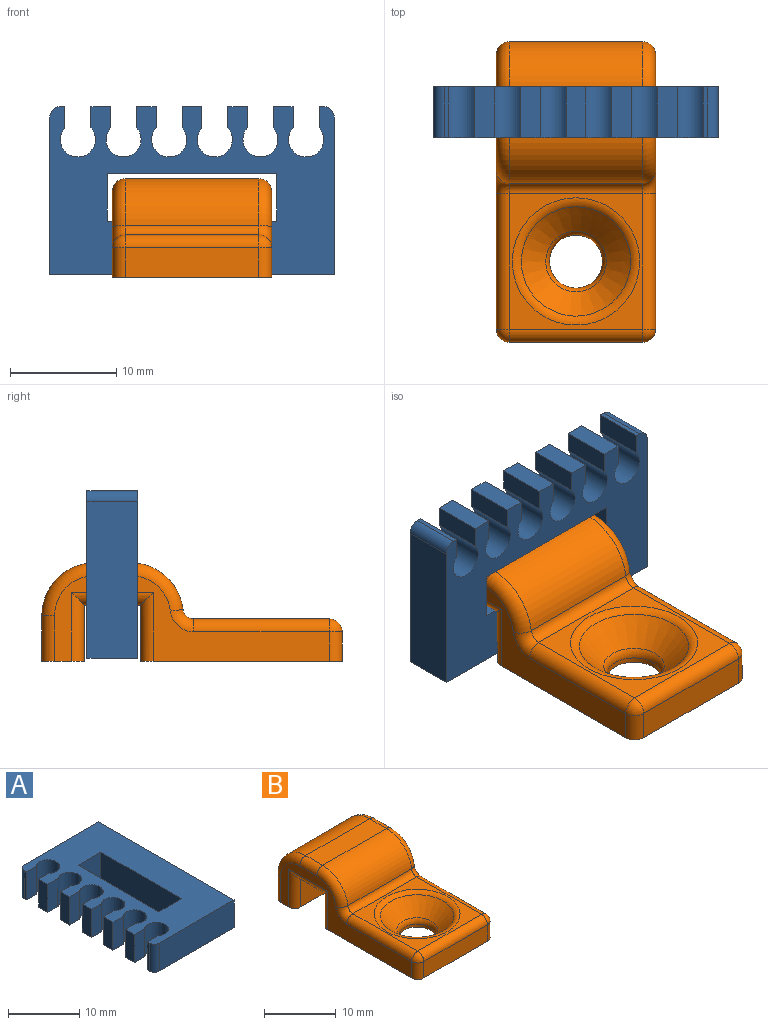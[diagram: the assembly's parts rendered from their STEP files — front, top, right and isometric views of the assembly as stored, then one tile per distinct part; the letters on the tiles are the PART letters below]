
ASSEMBLY  parts=2 mates=1
PART A: 36 faces, bbox 15.8x26.8x4.8 mm
  f0: plane 14.8x4.8mm, normal (0,-1,0), area 71mm2, adj f2,f3,f29,f31
  f1: plane 14.8x4.8mm, normal (0,1,0), area 71mm2, adj f2,f3,f30,f31
  f2: plane 26.8x15.8mm, normal (0,0,1), area 275.8mm2, adj f0,f1,f4,f5,f6,f7,f8,f9
  f3: plane 26.8x15.8mm, normal (0,0,-1), area 275.8mm2, adj f0,f1,f4,f5,f6,f7,f8,f9
  f4: extruded ~4.8x3.3mm, area 36.4mm2, adj f2,f3,f12,f27
  f5: extruded ~4.8x3.3mm, area 36.4mm2, adj f2,f3,f24,f26
  f6: extruded ~4.8x3.3mm, area 36.4mm2, adj f2,f3,f21,f23
  f7: extruded ~4.8x3.3mm, area 36.4mm2, adj f2,f3,f18,f20
  f8: extruded ~4.8x3.3mm, area 36.4mm2, adj f2,f3,f15,f17
  f9: extruded ~4.8x3.3mm, area 36.4mm2, adj f2,f3,f10,f14
  f10: plane 4.8x2mm, normal (0,1,0), area 9.6mm2, adj f2,f3,f9,f11
  f11: plane 4.8x0.42mm, normal (-1,0,0), area 2mm2, adj f2,f3,f10,f29
  f12: plane 4.8x2mm, normal (0,-1,0), area 9.6mm2, adj f2,f3,f4,f13
  f13: plane 4.8x0.42mm, normal (-1,0,0), area 2mm2, adj f2,f3,f12,f30
  f14: plane 4.8x2mm, normal (0,-1,0), area 9.6mm2, adj f2,f3,f9,f16
  f15: plane 4.8x2mm, normal (0,1,0), area 9.6mm2, adj f2,f3,f8,f16
  f16: plane 4.8x1.84mm, normal (-1,0,0), area 8.8mm2, adj f2,f3,f14,f15
  f17: plane 4.8x2mm, normal (0,-1,0), area 9.6mm2, adj f2,f3,f8,f19
  f18: plane 4.8x2mm, normal (0,1,0), area 9.6mm2, adj f2,f3,f7,f19
  f19: plane 4.8x1.84mm, normal (-1,0,0), area 8.8mm2, adj f2,f3,f17,f18
  f20: plane 4.8x2mm, normal (0,-1,0), area 9.6mm2, adj f2,f3,f7,f22
  f21: plane 4.8x2mm, normal (0,1,0), area 9.6mm2, adj f2,f3,f6,f22
  f22: plane 4.8x1.84mm, normal (-1,0,0), area 8.8mm2, adj f2,f3,f20,f21
  f23: plane 4.8x2mm, normal (0,-1,0), area 9.6mm2, adj f2,f3,f6,f25
  f24: plane 4.8x2mm, normal (0,1,0), area 9.6mm2, adj f2,f3,f5,f25
  f25: plane 4.8x1.84mm, normal (-1,0,0), area 8.8mm2, adj f2,f3,f23,f24
  f26: plane 4.8x2mm, normal (0,-1,0), area 9.6mm2, adj f2,f3,f5,f28
  f27: plane 4.8x2mm, normal (0,1,0), area 9.6mm2, adj f2,f3,f4,f28
  f28: plane 4.8x1.84mm, normal (-1,0,0), area 8.8mm2, adj f2,f3,f26,f27
  f29: cylinder r=1mm len=4.8mm, axis (0,0,1), area 7.5mm2, adj f0,f2,f3,f11
  f30: cylinder r=1mm len=4.8mm, axis (0,0,-1), area 7.5mm2, adj f1,f2,f3,f13
  f31: plane 26.8x4.8mm, normal (1,0,0), area 128.6mm2, adj f0,f1,f2,f3
  f32: plane 4.8x4.5mm, normal (0,-1,0), area 21.6mm2, adj f2,f3,f33,f34
  f33: plane 16x4.8mm, normal (-1,0,0), area 76.8mm2, adj f2,f3,f32,f35
  f34: plane 16x4.8mm, normal (1,0,0), area 76.8mm2, adj f2,f3,f32,f35
  f35: plane 4.8x4.5mm, normal (0,1,0), area 21.6mm2, adj f2,f3,f33,f34
PART B: 41 faces, bbox 15x28.7x10.1 mm
  f0: plane 12.6x2.8mm, normal (0,-1,0), area 35.3mm2, adj f1,f21,f24,f25
  f1: plane 19x15mm, normal (0,0,-1), area 264.1mm2, adj f0,f2,f9,f10,f14,f21,f24,f35
  f2: plane 12.6x5.3mm, normal (0,1,0), area 66.8mm2, adj f1,f3,f35,f38
  f3: plane 12.6x5.3mm, normal (0,0,-1), area 66.8mm2, adj f2,f4,f36,f39
  f4: plane 12.6x5.3mm, normal (0,-1,0), area 66.8mm2, adj f3,f5,f37,f40
  f5: plane 15x4mm, normal (0,0,-1), area 58.8mm2, adj f4,f6,f9,f10,f16,f32,f37,f40
  f6: plane 12.6x4.3mm, normal (0,1,0), area 54.2mm2, adj f5,f12,f16,f32
  f7: plane 12.6x3.34mm, normal (0,0,1), area 42.1mm2, adj f12,f13,f18,f30
  f8: plane 12.8x12.6mm, normal (0,0,1), area 48.3mm2, adj f11,f22,f25,f27,f33
  f9: plane 25.9x8.1mm, normal (1,0,0), area 75.2mm2, adj f1,f5,f24,f27,f28,f29,f30,f31
  f10: plane 25.9x8.1mm, normal (-1,0,0), area 75.2mm2, adj f1,f5,f16,f17,f18,f19,f20,f21
  f11: cylinder r=1mm len=12.6mm, axis (1,0,0), area 18.3mm2, adj f8,f13,f20,f28
  f12: cylinder r=5mm len=12.6mm, axis (-1,0,0), area 99mm2, adj f6,f7,f17,f31
  f13: cylinder r=5mm len=12.6mm, axis (1,0,0), area 91.6mm2, adj f7,f11,f19,f29
  f14: cylinder r=2.5mm len=5mm, axis (0,0,1), area 7.9mm2, adj f1,f34
  f15: cone r=2.5mm half-angle=45deg, axis (0,0,1), area 81.6mm2, adj f33,f34
  f16: cylinder r=1.2mm len=4.3mm, axis (0,0,1), area 8.1mm2, adj f5,f6,f10,f17
  f17: torus R=3.8mm, axis (1,0,0), area 13.5mm2, adj f10,f12,f16,f18
  f18: cylinder r=1.2mm len=3.34mm, axis (0,-1,0), area 6.3mm2, adj f7,f10,f17,f19
  f19: torus R=3.8mm, axis (1,0,0), area 12.5mm2, adj f10,f13,f18,f20
  f20: torus R=2.2mm, axis (1,0,0), area 3.9mm2, adj f10,f11,f19,f22
  f21: cylinder r=1.2mm len=2.8mm, axis (0,0,-1), area 5.3mm2, adj f0,f1,f10,f23
  f22: cylinder r=1.2mm len=12.8mm, axis (0,-1,0), area 24.1mm2, adj f8,f10,f20,f23
  f23: sphere r=1.2mm, area 2.3mm2, adj f21,f22,f25
  f24: cylinder r=1.2mm len=2.8mm, axis (0,0,1), area 5.3mm2, adj f0,f1,f9,f26
  f25: cylinder r=1.2mm len=12.6mm, axis (-1,0,0), area 23.8mm2, adj f0,f8,f23,f26
  f26: sphere r=1.2mm, area 2.3mm2, adj f24,f25,f27
  f27: cylinder r=1.2mm len=12.8mm, axis (0,1,0), area 24.1mm2, adj f8,f9,f26,f28
  f28: torus R=2.2mm, axis (1,0,0), area 3.9mm2, adj f9,f11,f27,f29
  f29: torus R=3.8mm, axis (1,0,0), area 12.5mm2, adj f9,f13,f28,f30
  f30: cylinder r=1.2mm len=3.34mm, axis (0,1,0), area 6.3mm2, adj f7,f9,f29,f31
  f31: torus R=3.8mm, axis (1,0,0), area 13.5mm2, adj f9,f12,f30,f32
  f32: cylinder r=1.2mm len=4.3mm, axis (0,0,-1), area 8.1mm2, adj f5,f6,f9,f31
  f33: torus R=6mm, axis (0,0,-1), area 32.9mm2, adj f8,f15
  f34: torus R=3.7mm, axis (0,0,-1), area 15.5mm2, adj f14,f15
  f35: cylinder r=1.2mm len=6.5mm, axis (0,0,1), area 10.8mm2, adj f1,f2,f10,f36
  f36: cylinder r=1.2mm len=7.7mm, axis (0,1,0), area 11.6mm2, adj f3,f10,f35,f37
  f37: cylinder r=1.2mm len=6.5mm, axis (0,0,-1), area 10.8mm2, adj f4,f5,f10,f36
  f38: cylinder r=1.2mm len=6.5mm, axis (0,0,-1), area 10.8mm2, adj f1,f2,f9,f39
  f39: cylinder r=1.2mm len=7.7mm, axis (0,-1,0), area 11.6mm2, adj f3,f9,f38,f40
  f40: cylinder r=1.2mm len=6.5mm, axis (0,0,1), area 10.8mm2, adj f4,f5,f9,f39
PLACE A rot(axis=(-0.58,0.58,0.58),120deg) t=(14.5,-15.92,17.81)mm
PLACE B t=(-6.4,-10.87,1.33)mm
MATE fastened A.f33 <-> B.f3  axis (0,0,1) through (1.1,-13.52,9.01)mm
